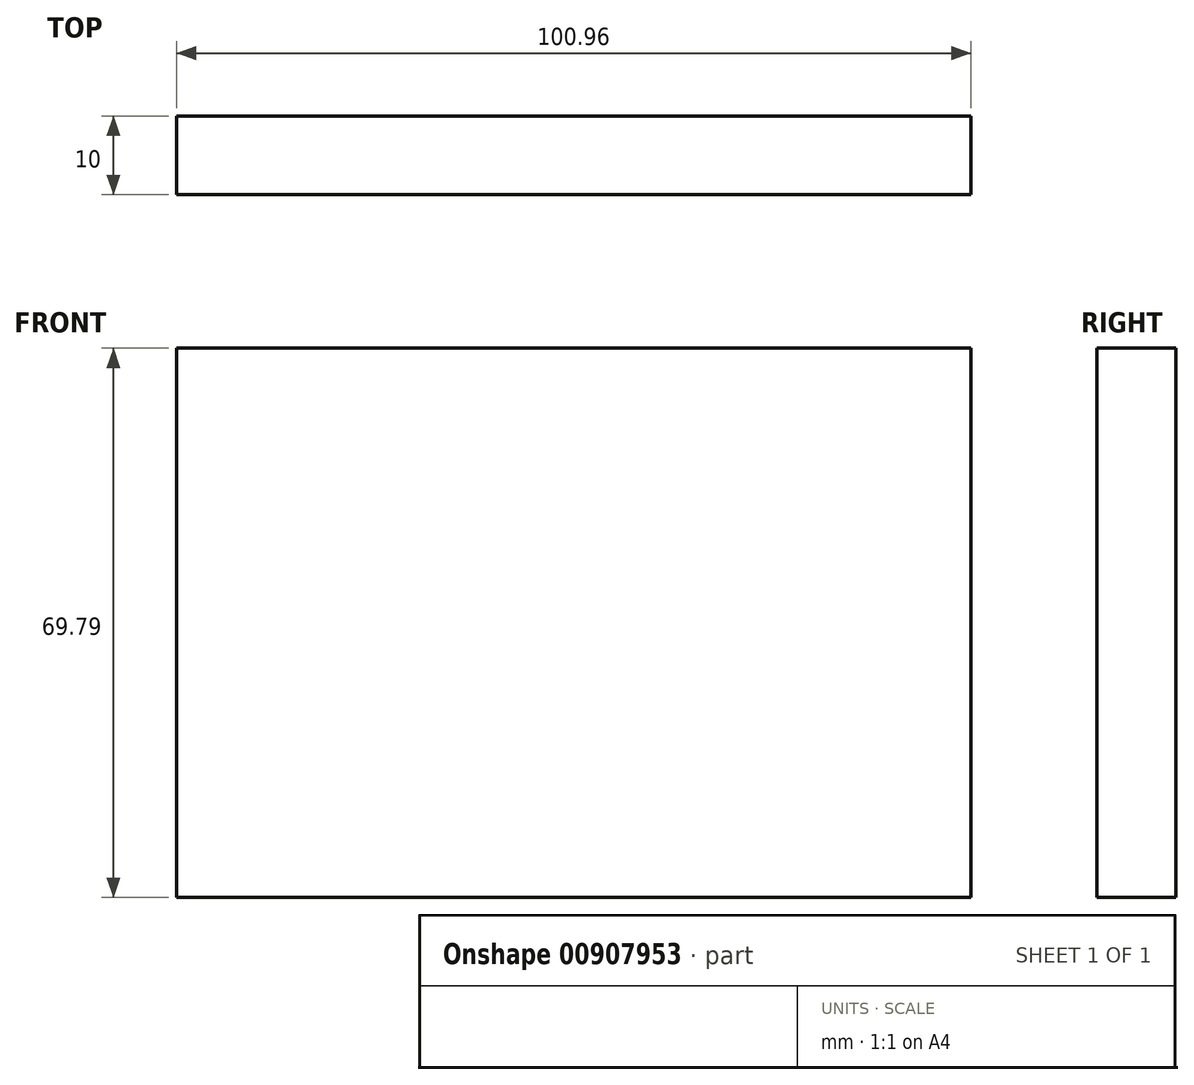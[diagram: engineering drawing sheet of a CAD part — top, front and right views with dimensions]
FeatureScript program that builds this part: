
annotation { "Feature Type Name" : "Feature", "Feature Type Description" : "" }
export const myFeature = defineFeature(function(context is Context, id is Id, definition is map)
    precondition{}
    {
        {
            var Q0;
            Q0=qCreatedBy(makeId("Front.planeOp"),FACE);
            var sketch = newSketch(context, id + "F0", { "sketchPlane" : qUnion([Q0])});
            skLineSegment(sketch, "E0.bottom", {"start": v(-41.7, 31.44) * mm, "end": v(59.25, 31.44) * mm});
            skLineSegment(sketch, "E0.top", {"start": v(-41.7, -38.35) * mm, "end": v(59.25, -38.35) * mm});
            skLineSegment(sketch, "E0.left", {"start": v(-41.7, 31.44) * mm, "end": v(-41.7, -38.35) * mm});
            skLineSegment(sketch, "E0.right", {"start": v(59.25, 31.44) * mm, "end": v(59.25, -38.35) * mm});
            skSolve(sketch);
        }
        {
            var Q0;
            Q0=makeQuery(id+"F0.imprint","IMPRINT",FACE,{"disambiguationData":[TD([[makeQuery(id+"F0.imprint","IMPRINT",EDGE,{"derivedFrom":sQuery(id+"F0.wireOp",EDGE,"E0.bottom")}),-1.0]])]});
            extrude(context, id + "F1", {"entities" : qUnion([Q0]), "depth" : 10 * mm, "offsetDistance" : 25 * mm});
        }
    });
